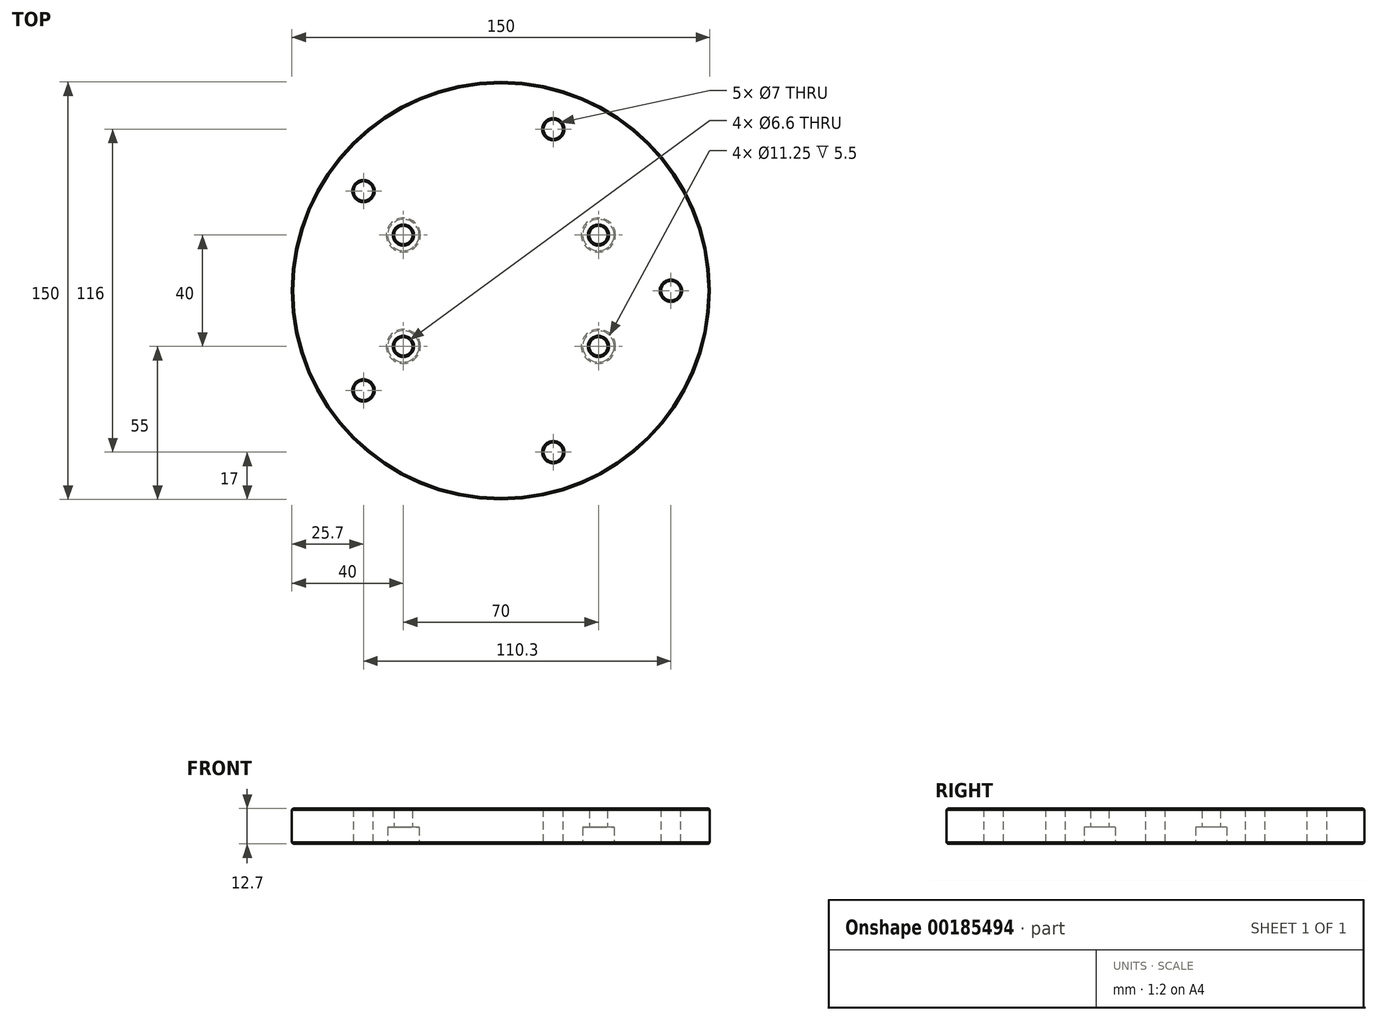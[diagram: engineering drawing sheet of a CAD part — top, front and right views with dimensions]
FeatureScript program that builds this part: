
annotation { "Feature Type Name" : "Feature", "Feature Type Description" : "" }
export const myFeature = defineFeature(function(context is Context, id is Id, definition is map)
    precondition{}
    {
        {
            var Q0;
            Q0=qCreatedBy(makeId("Top.planeOp"),FACE);
            var sketch = newSketch(context, id + "F0", { "sketchPlane" : qUnion([Q0])});
            skCircle(sketch, "E0", {"center": v(0, 0) * mm, "radius": 75 * mm});
            skPoint(sketch, "E1", {"position": v(-20, 35) * mm});
            skPoint(sketch, "E2", {"position": v(20, 35) * mm});
            skPoint(sketch, "E3", {"position": v(-20, -35) * mm});
            skPoint(sketch, "E4", {"position": v(20, -35) * mm});
            skSolve(sketch);
        }
        {
            var Q0;
            Q0=makeQuery(id+"F0.imprint","IMPRINT",FACE,{"disambiguationData":[TD([[makeQuery(id+"F0.imprint","IMPRINT",EDGE,{"derivedFrom":sQuery(id+"F0.wireOp",EDGE,"E0")}),1.0]])]});
            extrude(context, id + "F1", {"entities" : qUnion([Q0]), "depth" : 12.7 * mm});
        }
        {
            var Q0;
            Q0=sQuery(id+"F0.wireOp",VERTEX,"E1");
            var Q1;
            Q1=sQuery(id+"F0.wireOp",VERTEX,"E2");
            var Q2;
            Q2=sQuery(id+"F0.wireOp",VERTEX,"E3");
            var Q3;
            Q3=sQuery(id+"F0.wireOp",VERTEX,"E4");
            var Q4;
            Q4=makeQuery(id+"F1.opExtrude","SWEPT_BODY",BODY,{"disambiguationData":[OSD([sQuery(id+"F0.wireOp",EDGE,"E0")])]});
            hole(context, id + "F2", {"style" : HoleStyle.C_BORE, "endStyle" : HoleEndStyle.THROUGH, "oppositeDirection" : true, "standardTappedOrClearance" : lookupTablePath({ "fit" : "Normal", "standard" : "ISO", "size" : "M6", "type" : "Clearance" }), "standardBlindInLast" : lookupTablePath({ "fit" : "Normal", "standard" : "ISO", "engagement" : "75%", "pitch" : "1 mm", "size" : "M6", "type" : "Clearance & tapped" }), "holeDiameter" : 6.6 * mm, "cBoreDiameter" : 11.25 * mm, "cBoreDepth" : 6 * mm, "majorDiameter" : 5 * mm, "startFromSketch" : true, "locations" : qUnion([Q0, Q1, Q2, Q3]), "scope" : qUnion([Q4]), "isTappedThrough" : true, "tappedDepth" : 12 * mm, "tapClearance" : 3});
        }
        {
            var Q0;
            Q0=makeQuery(id+"F1.opExtrude","CAP_FACE",FACE,{"disambiguationData":[OSD([sQuery(id+"F0.wireOp",EDGE,"E0")])],"isStart":false});
            var sketch = newSketch(context, id + "F3", { "sketchPlane" : qUnion([Q0])});
            skPoint(sketch, "E5", {"position": v(58, 18.8) * mm});
            skPoint(sketch, "E6", {"position": v(-58, 18.8) * mm});
            skPoint(sketch, "E7", {"position": v(0, 61) * mm});
            skPoint(sketch, "E8", {"position": v(35.8, -49.3) * mm});
            skPoint(sketch, "E9", {"position": v(-35.8, -49.3) * mm});
            skSolve(sketch);
        }
        {
            var Q0;
            Q0=sQuery(id+"F3.wireOp",VERTEX,"E7");
            var Q1;
            Q1=sQuery(id+"F3.wireOp",VERTEX,"E5");
            var Q2;
            Q2=sQuery(id+"F3.wireOp",VERTEX,"E8");
            var Q3;
            Q3=sQuery(id+"F3.wireOp",VERTEX,"E9");
            var Q4;
            Q4=sQuery(id+"F3.wireOp",VERTEX,"E6");
            var Q5;
            Q5=makeQuery(id+"F1.opExtrude","SWEPT_BODY",BODY,{"disambiguationData":[OSD([sQuery(id+"F0.wireOp",EDGE,"E0")])]});
            hole(context, id + "F4", {"style" : HoleStyle.SIMPLE, "endStyle" : HoleEndStyle.THROUGH, "standardTappedOrClearance" : lookupTablePath({ "standard" : "ISO", "engagement" : "75%", "pitch" : "1 mm", "size" : "M8", "type" : "Tapped" }), "standardBlindInLast" : lookupTablePath({ "standard" : "ISO", "engagement" : "75%", "pitch" : "1 mm", "size" : "M8", "type" : "Tapped" }), "holeDiameter" : 7 * mm, "startFromSketch" : true, "locations" : qUnion([Q0, Q1, Q2, Q3, Q4]), "scope" : qUnion([Q5]), "isTappedThrough" : true, "majorDiameter" : 8 * mm, "showTappedDepth" : true});
        }
        {
            var Q0;
            Q0=makeQuery(id+"F1.opExtrude","CAP_FACE",FACE,{"disambiguationData":[OSD([sQuery(id+"F0.wireOp",EDGE,"E0")])],"isStart":false});
            var Q1;
            Q1=makeQuery(id+"F1.opExtrude","CAP_FACE",FACE,{"disambiguationData":[OSD([sQuery(id+"F0.wireOp",EDGE,"E0")])],"isStart":true});
            chamfer(context, id + "F5", {"entities" : qUnion([Q0, Q1]), "width" : .5 * mm, "tangentPropagation" : true});
        }
        {
            var Q0;
            Q0=qCreatedBy(makeId("Front.planeOp"),FACE);
            var sketch = newSketch(context, id + "F6", { "sketchPlane" : qUnion([Q0])});
            skLineSegment(sketch, "E10", {"start": v(0, -15.93) * mm, "end": v(0, 25.6) * mm, "construction": true});
            skSolve(sketch);
        }
        {
            var Q0;
            Q0=makeQuery(id+"F1.opExtrude","SWEPT_BODY",BODY,{"disambiguationData":[OSD([sQuery(id+"F0.wireOp",EDGE,"E0")])]});
            var Q1;
            Q1=sQuery(id+"F6.wireOp",EDGE,"E10");
            transform(context, id + "F7", {"entities" : qUnion([Q0]), "transformType" : TransformType.ROTATION, "transformAxis" : qUnion([Q1]), "angle" : 90 * degree, "oppositeDirection" : true, "makeCopy" : false});
        }
    });
